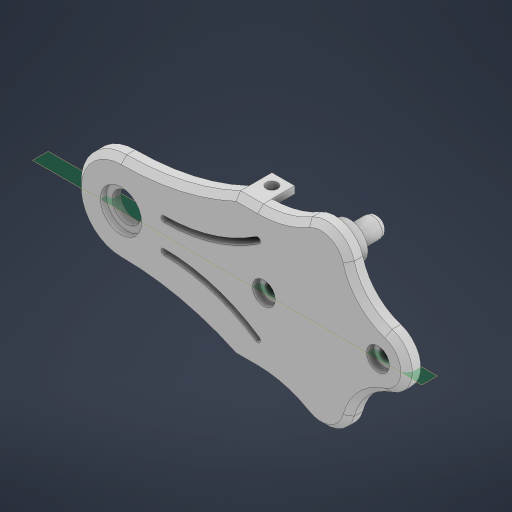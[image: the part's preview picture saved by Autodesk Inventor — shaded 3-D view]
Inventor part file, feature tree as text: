
AUTODESK INVENTOR PART (.ipt)
format: ipt  version: 2024.2 (Build 282272000, 272)  size: 813,568 bytes
history: native  units: in
note: dims shown in document units (in); Inventor stores cm internally (conversion verified against a paired STEP export)
features: extrude x12, sketch x10, projected_geometry x7, mirror x3, plane x1, fillet x1, chamfer x1
ambient origin geometry x8: Origin, YZ Plane, XZ Plane, XY Plane, X Axis, Y Axis, Z Axis, Center Point
bodies: Solid1 (feature_tree)
feature tree (35):
  extrude  "Extrusion1"  Depth=1.9685in
  plane  "Work Plane1"
  extrude  "Extrusion3"  Depth=0.1969in TaperAngle=0.0deg
  mirror  "Mirror1"
  extrude  "Extrusion4"  Depth=0.1575in
  extrude  "Extrusion5"  Depth=0.3677in
  mirror  "Mirror2"
  sketch  "Sketch7"  dims[d16=0.0787in d17=0.3937in]
  extrude  "Extrusion6"  Depth=0.3937in
  extrude  "Extrusion7"  Depth=0.5906in
  extrude  "Extrusion8"  TaperAngle=0.0deg  [1 undecoded]
  fillet  "Fillet1"  Radius=0.315in
  extrude  "Extrusion9"  Depth=0.315in TaperAngle=0.0deg
  mirror  "Mirror3"
  extrude  "Extrusion10"  Depth=0.1575in
  extrude  "Extrusion11"  Depth=0.3937in
  sketch  "Sketch12"  dims[d29=0.315in d30=0.0in d31=0.7874in d32=0.8268in d33=0.3937in d34=0.0in d35=0.5118in d36=0.1969in d37=0.0in d38=0.2756in d39=0.3937in d40=0.0in d41=0.0787in d42=0.0in d43=0.0in d44=0.6299in d45=0.315in d46=0.0984in d47=0.0in d48=0.5697in d49=0.0787in d50=0.0in d51=0.0787in d52=0.0787in d53=45.0deg d54=0.7874in d55=0.7874in d56=0.7874in d57=0.1575in d58=0.7874in d59=0.7874in d60=0.3937in d61=0.0in d62=0.3937in d63=0.0in]
  extrude  "Extrusion12"  Depth=0.3937in
  extrude  "Extrusion13"  Depth=0.3937in TaperAngle=0.0deg
  chamfer  "Chamfer1"  Distance=0.5118in
  sketch  "Sketch1"  dims[d1=0.4in d3=1.9685in]
  sketch  "Sketch4"  dims[d4=2.3441in d5=0.1969in d6=0.0in]
  sketch  "Sketch5"  dims[d12=0.1575in d13=1.5748in]
  projected_geometry  "Projected Loop1"
  sketch  "Sketch6"  dims[d14=1.971in d15=0.3677in]
  projected_geometry  "Projected Loop2"
  projected_geometry  "Projected Loop3"
  sketch  "Sketch8"  dims[d18=0.315in d19=0.5906in]
  projected_geometry  "Projected Loop4"
  sketch  "Sketch9"  dims[d20=0.1969in d21=0.0in d22=0.0in d23=0.315in]
  projected_geometry  "Projected Loop5"
  sketch  "Sketch10"  dims[d24=0.0984in d25=0.315in d26=0.0in]
  projected_geometry  "Projected Loop6"
  sketch  "Sketch11"  dims[d27=0.1575in d28=0.1575in]
  projected_geometry  "Projected Loop7"
note: 1 required parameter value undecoded (feature->parameter linkage not recoverable at this tier; creation-order binding heuristic only, values carry confidence <= 0.55)
